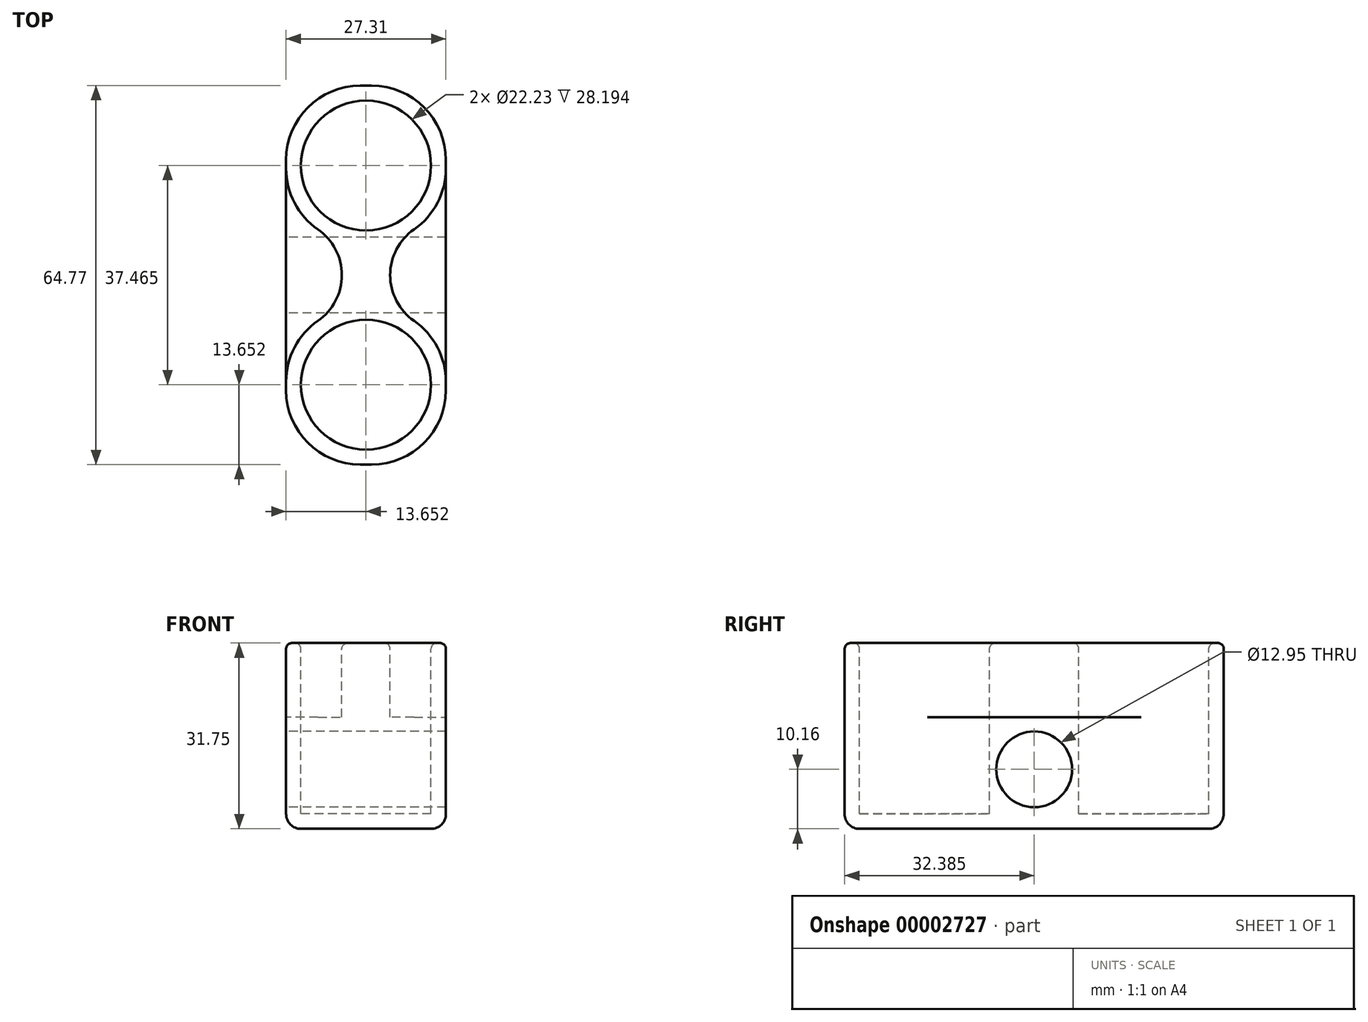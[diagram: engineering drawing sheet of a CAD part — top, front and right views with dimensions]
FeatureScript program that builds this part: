
annotation { "Feature Type Name" : "Feature", "Feature Type Description" : "" }
export const myFeature = defineFeature(function(context is Context, id is Id, definition is map)
    precondition{}
    {
        {
            var Q0;
            Q0=qCreatedBy(makeId("Top.planeOp"),FACE);
            var sketch = newSketch(context, id + "F0", { "sketchPlane" : qUnion([Q0])});
            skLineSegment(sketch, "E0.bottom", {"start": v(0, 0) * mm, "end": v(27.3, 0) * mm});
            skLineSegment(sketch, "E0.top", {"start": v(0, -64.77) * mm, "end": v(27.3, -64.77) * mm});
            skLineSegment(sketch, "E0.left", {"start": v(0, 0) * mm, "end": v(0, -64.77) * mm});
            skLineSegment(sketch, "E0.right", {"start": v(27.3, 0) * mm, "end": v(27.3, -64.77) * mm});
            skSolve(sketch);
        }
        {
            var Q0;
            Q0=makeQuery(id+"F0.imprint","IMPRINT",FACE,{"disambiguationData":[TD([[makeQuery(id+"F0.imprint","IMPRINT",EDGE,{"derivedFrom":sQuery(id+"F0.wireOp",EDGE,"E0.bottom")}),-1.0]])]});
            extrude(context, id + "F1", {"entities" : qUnion([Q0]), "depth" : 31.75 * mm});
        }
        {
            var Q0;
            Q0=makeQuery(id+"F1.opExtrude","CAP_FACE",FACE,{"disambiguationData":[OSD([sQuery(id+"F0.wireOp",EDGE,"E0.bottom"),sQuery(id+"F0.wireOp",EDGE,"E0.top"),sQuery(id+"F0.wireOp",EDGE,"E0.left"),sQuery(id+"F0.wireOp",EDGE,"E0.right")])],"isStart":false});
            var sketch = newSketch(context, id + "F2", { "sketchPlane" : qUnion([Q0])});
            skLineSegment(sketch, "E1", {"start": v(13.65, 0) * mm, "end": v(13.65, -64.77) * mm, "construction": true});
            skLineSegment(sketch, "E2", {"start": v(0, 0) * mm, "end": v(0, -13.65) * mm, "construction": true});
            skLineSegment(sketch, "E3", {"start": v(0, -13.65) * mm, "end": v(13.65, -13.65) * mm, "construction": true});
            skLineSegment(sketch, "E4", {"start": v(0, -64.77) * mm, "end": v(0, -51.12) * mm, "construction": true});
            skLineSegment(sketch, "E5", {"start": v(0, -51.12) * mm, "end": v(13.65, -51.12) * mm, "construction": true});
            skSolve(sketch);
        }
        {
            var Q0;
            Q0=makeQuery(id+"F2.imprint","IMPRINT",FACE,{"disambiguationData":[TD([[makeQuery(id+"F2.imprint","IMPRINT",EDGE,{"derivedFrom":makeQuery(id+"F1.opExtrude","CAP_EDGE",EDGE,{"disambiguationData":[OSD([sQuery(id+"F0.wireOp",EDGE,"E0.bottom")])],"isStart":false})}),-1.0]])]});
            var sketch = newSketch(context, id + "F3", { "sketchPlane" : qUnion([Q0])});
            skCircle(sketch, "E6", {"center": v(13.65, -13.65) * mm, "radius": 11.11 * mm});
            skCircle(sketch, "E7", {"center": v(13.65, -51.12) * mm, "radius": 11.11 * mm});
            skSolve(sketch);
        }
        {
            var Q0;
            {Q0=qUnion([makeQuery(id+"F3.imprint","IMPRINT",FACE,{"disambiguationData":[TD([[makeQuery(id+"F3.imprint","IMPRINT",EDGE,{"derivedFrom":sQuery(id+"F3.wireOp",EDGE,"E6")}),1.0]])]}),makeQuery(id+"F3.imprint","IMPRINT",FACE,{"disambiguationData":[TD([[makeQuery(id+"F3.imprint","IMPRINT",EDGE,{"derivedFrom":sQuery(id+"F3.wireOp",EDGE,"E7")}),1.0]])]})]);}
            extrude(context, id + "F4", {"entities" : qUnion([Q0]), "operationType" : NewBodyOperationType.REMOVE, "oppositeDirection" : true, "depth" : 29.2 * mm});
        }
        {
            var Q0;
            Q0=makeQuery(id+"F1.opExtrude","SWEPT_EDGE",EDGE,{"disambiguationData":[OSD([sQuery(id+"F0.wireOp",EDGE,"E0.bottom"),sQuery(id+"F0.wireOp",EDGE,"E0.right")])]});
            var Q1;
            Q1=makeQuery(id+"F1.opExtrude","SWEPT_EDGE",EDGE,{"disambiguationData":[OSD([sQuery(id+"F0.wireOp",EDGE,"E0.top"),sQuery(id+"F0.wireOp",EDGE,"E0.right")])]});
            var Q2;
            Q2=makeQuery(id+"F1.opExtrude","SWEPT_EDGE",EDGE,{"disambiguationData":[OSD([sQuery(id+"F0.wireOp",EDGE,"E0.top"),sQuery(id+"F0.wireOp",EDGE,"E0.left")])]});
            var Q3;
            Q3=makeQuery(id+"F1.opExtrude","SWEPT_EDGE",EDGE,{"disambiguationData":[OSD([sQuery(id+"F0.wireOp",EDGE,"E0.bottom"),sQuery(id+"F0.wireOp",EDGE,"E0.left")])]});
            fillet(context, id + "F5", {"entities" : qUnion([Q0, Q1, Q2, Q3]), "radius" : 12.7 * mm, "tangentPropagation" : true, "allowEdgeOverflow" : false});
        }
        {
            var Q0;
            Q0=makeQuery(id+"F2.imprint","IMPRINT",FACE,{"disambiguationData":[TD([[makeQuery(id+"F2.imprint","IMPRINT",EDGE,{"derivedFrom":makeQuery(id+"F1.opExtrude","CAP_EDGE",EDGE,{"disambiguationData":[OSD([sQuery(id+"F0.wireOp",EDGE,"E0.bottom")])],"isStart":false})}),-1.0]])]});
            var sketch = newSketch(context, id + "F6", { "sketchPlane" : qUnion([Q0])});
            skCircle(sketch, "E8", {"center": v(0, -32.39) * mm, "radius": 9.53 * mm});
            skLineSegment(sketch, "E9", {"start": v(0, -32.39) * mm, "end": v(27.3, -32.39) * mm, "construction": true});
            skCircle(sketch, "E10", {"center": v(27.3, -32.39) * mm, "radius": 9.53 * mm});
            skSolve(sketch);
        }
        {
            var Q0;
            {var subQ0=makeQuery(id+"F2.imprint","IMPRINT",EDGE,{"derivedFrom":makeQuery(id+"F1.opExtrude","CAP_EDGE",EDGE,{"disambiguationData":[OSD([sQuery(id+"F0.wireOp",EDGE,"E0.left")])],"isStart":false})});var subQ1=sQuery(id+"F6.wireOp",EDGE,"E8");var subQ3=makeQuery(id+"F6.imprint","INTERSECT",VERTEX,{"disambiguationData":[OD(0.0)],"derivedFrom":[subQ0,subQ1]});var subQ5=makeQuery(id+"F2.imprint","IMPRINT",EDGE,{"derivedFrom":makeQuery(id+"F1.opExtrude","CAP_EDGE",EDGE,{"disambiguationData":[OSD([sQuery(id+"F0.wireOp",EDGE,"E0.right")])],"isStart":false})});var subQ6=sQuery(id+"F6.wireOp",EDGE,"E10");var subQ8=makeQuery(id+"F6.imprint","INTERSECT",VERTEX,{"disambiguationData":[OD(0.0)],"derivedFrom":[subQ5,subQ6]});Q0=qUnion([makeQuery(id+"F6.imprint","IMPRINT",FACE,{"disambiguationData":[TD([[makeQuery(id+"F6.imprint","IMPRINT",EDGE,{"disambiguationData":[TD([[subQ3,-1.0]])],"derivedFrom":subQ1}),1.0]])]}),makeQuery(id+"F6.imprint","IMPRINT",FACE,{"disambiguationData":[TD([[makeQuery(id+"F6.imprint","IMPRINT",EDGE,{"disambiguationData":[TD([[subQ8,1.0]])],"derivedFrom":subQ6}),1.0]])]}),makeQuery(id+"F6.imprint","IMPRINT",FACE,{"disambiguationData":[TD([[makeQuery(id+"F6.imprint","IMPRINT",EDGE,{"disambiguationData":[TD([[subQ3,1.0]])],"derivedFrom":subQ1}),1.0]])]}),makeQuery(id+"F6.imprint","IMPRINT",FACE,{"disambiguationData":[TD([[makeQuery(id+"F6.imprint","IMPRINT",EDGE,{"disambiguationData":[TD([[subQ8,-1.0]])],"derivedFrom":subQ6}),1.0]])]})]);}
            extrude(context, id + "F7", {"entities" : qUnion([Q0]), "operationType" : NewBodyOperationType.REMOVE, "oppositeDirection" : true, "depth" : 12.7 * mm});
        }
        {
            var Q0;
            Q0=makeQuery(id+"F7.boolean.opBoolean","INTERSECT",EDGE,{"disambiguationData":[OD(0.0)],"derivedFrom":[makeQuery(id+"F1.opExtrude","SWEPT_FACE",FACE,{"disambiguationData":[OSD([sQuery(id+"F0.wireOp",EDGE,"E0.left")])]}),makeQuery(id+"F7.opExtrude","SWEPT_FACE",FACE,{"disambiguationData":[OSD([sQuery(id+"F6.wireOp",EDGE,"E8")])]})]});
            var Q1;
            Q1=makeQuery(id+"F7.boolean.opBoolean","INTERSECT",EDGE,{"disambiguationData":[OD(1.0)],"derivedFrom":[makeQuery(id+"F1.opExtrude","SWEPT_FACE",FACE,{"disambiguationData":[OSD([sQuery(id+"F0.wireOp",EDGE,"E0.left")])]}),makeQuery(id+"F7.opExtrude","SWEPT_FACE",FACE,{"disambiguationData":[OSD([sQuery(id+"F6.wireOp",EDGE,"E8")])]})]});
            var Q2;
            Q2=makeQuery(id+"F7.boolean.opBoolean","INTERSECT",EDGE,{"disambiguationData":[OD(0.0)],"derivedFrom":[makeQuery(id+"F1.opExtrude","SWEPT_FACE",FACE,{"disambiguationData":[OSD([sQuery(id+"F0.wireOp",EDGE,"E0.right")])]}),makeQuery(id+"F7.opExtrude","SWEPT_FACE",FACE,{"disambiguationData":[OSD([sQuery(id+"F6.wireOp",EDGE,"E10")])]})]});
            var Q3;
            Q3=makeQuery(id+"F7.boolean.opBoolean","INTERSECT",EDGE,{"disambiguationData":[OD(1.0)],"derivedFrom":[makeQuery(id+"F1.opExtrude","SWEPT_FACE",FACE,{"disambiguationData":[OSD([sQuery(id+"F0.wireOp",EDGE,"E0.right")])]}),makeQuery(id+"F7.opExtrude","SWEPT_FACE",FACE,{"disambiguationData":[OSD([sQuery(id+"F6.wireOp",EDGE,"E10")])]})]});
            fillet(context, id + "F8", {"entities" : qUnion([Q0, Q1, Q2, Q3]), "radius" : 12.7 * mm, "tangentPropagation" : true, "allowEdgeOverflow" : false});
        }
        {
            var Q0;
            Q0=makeQuery(id+"F1.opExtrude","CAP_FACE",FACE,{"disambiguationData":[OSD([sQuery(id+"F0.wireOp",EDGE,"E0.bottom"),sQuery(id+"F0.wireOp",EDGE,"E0.top"),sQuery(id+"F0.wireOp",EDGE,"E0.left"),sQuery(id+"F0.wireOp",EDGE,"E0.right")])],"isStart":false});
            fillet(context, id + "F9", {"entities" : qUnion([Q0]), "radius" : 1.02 * mm, "tangentPropagation" : true, "allowEdgeOverflow" : false});
        }
        {
            var Q0;
            Q0=makeQuery(id+"F1.opExtrude","CAP_FACE",FACE,{"disambiguationData":[OSD([sQuery(id+"F0.wireOp",EDGE,"E0.bottom"),sQuery(id+"F0.wireOp",EDGE,"E0.top"),sQuery(id+"F0.wireOp",EDGE,"E0.left"),sQuery(id+"F0.wireOp",EDGE,"E0.right")])],"isStart":true});
            fillet(context, id + "F10", {"entities" : qUnion([Q0]), "radius" : 2.54 * mm, "tangentPropagation" : true, "allowEdgeOverflow" : false});
        }
        {
            var Q0;
            Q0=makeQuery(id+"F1.opExtrude","SWEPT_FACE",FACE,{"disambiguationData":[OSD([sQuery(id+"F0.wireOp",EDGE,"E0.left")])]});
            var sketch = newSketch(context, id + "F11", { "sketchPlane" : qUnion([Q0])});
            skLineSegment(sketch, "E11", {"start": v(32.39, 2.54) * mm, "end": v(32.39, 10.16) * mm, "construction": true});
            skCircle(sketch, "E12", {"center": v(32.39, 10.16) * mm, "radius": 6.48 * mm});
            skSolve(sketch);
        }
        {
            var Q0;
            Q0=makeQuery(id+"F11.imprint","IMPRINT",FACE,{"disambiguationData":[TD([[makeQuery(id+"F11.imprint","IMPRINT",EDGE,{"derivedFrom":sQuery(id+"F11.wireOp",EDGE,"E12")}),1.0]])]});
            extrude(context, id + "F12", {"entities" : qUnion([Q0]), "operationType" : NewBodyOperationType.REMOVE, "oppositeDirection" : true, "depth" : 27.94 * mm});
        }
    });
